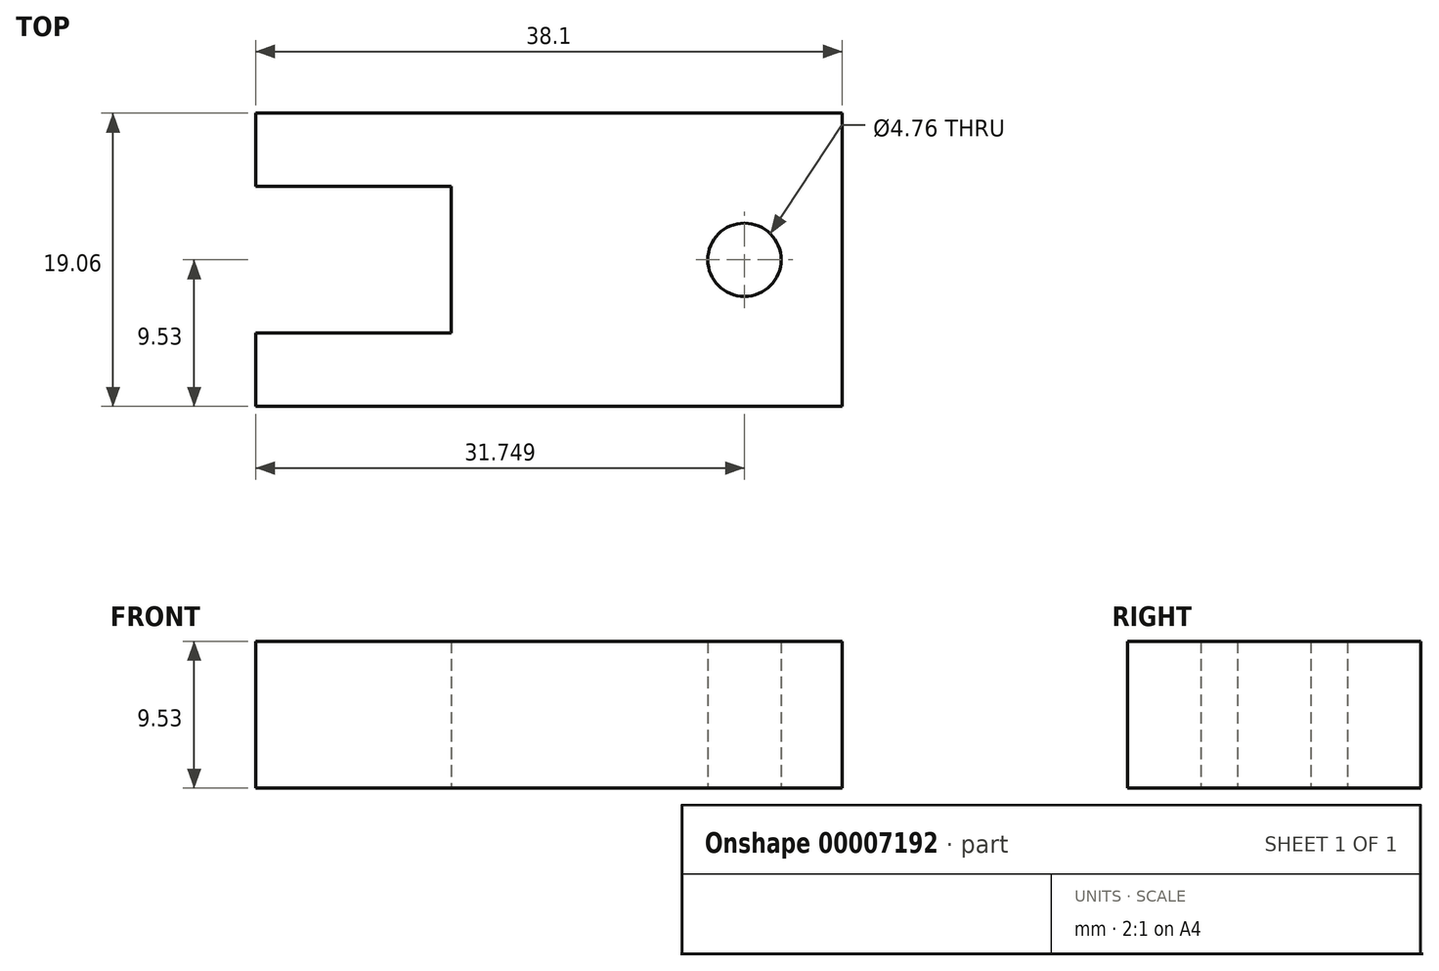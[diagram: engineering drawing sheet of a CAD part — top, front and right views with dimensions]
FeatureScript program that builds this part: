
annotation { "Feature Type Name" : "Feature", "Feature Type Description" : "" }
export const myFeature = defineFeature(function(context is Context, id is Id, definition is map)
    precondition{}
    {
        {
            var Q0;
            Q0=qCreatedBy(makeId("Top.planeOp"),FACE);
            var sketch = newSketch(context, id + "F0", { "sketchPlane" : qUnion([Q0])});
            skLineSegment(sketch, "E0", {"start": v(-14.22, 9.52) * mm, "end": v(-14.22, 4.76) * mm});
            skLineSegment(sketch, "E1", {"start": v(-14.22, 4.76) * mm, "end": v(-1.52, 4.76) * mm});
            skLineSegment(sketch, "E2", {"start": v(-1.52, 4.76) * mm, "end": v(-1.52, -4.76) * mm});
            skLineSegment(sketch, "E3", {"start": v(-1.52, -4.76) * mm, "end": v(-14.22, -4.76) * mm});
            skLineSegment(sketch, "E4", {"start": v(-14.22, -4.76) * mm, "end": v(-14.22, -9.52) * mm});
            skLineSegment(sketch, "E5", {"start": v(-14.22, -9.52) * mm, "end": v(23.88, -9.52) * mm});
            skLineSegment(sketch, "E6", {"start": v(23.88, -9.52) * mm, "end": v(23.88, 9.53) * mm});
            skLineSegment(sketch, "E7", {"start": v(23.88, 9.53) * mm, "end": v(-14.22, 9.52) * mm});
            skLineSegment(sketch, "E8", {"start": v(-23.53, 0) * mm, "end": v(23.87, 0) * mm});
            skCircle(sketch, "E9", {"center": v(17.53, 0) * mm, "radius": 2.38 * mm});
            skSolve(sketch);
        }
        {
            var Q0;
            {var subQ9=sQuery(id+"F0.wireOp",EDGE,"E3");Q0=makeQuery(id+"F0.imprint","IMPRINT",FACE,{"disambiguationData":[TD([[makeQuery(id+"F0.imprint","IMPRINT",EDGE,{"derivedFrom":subQ9}),1.0]])]});}
            var Q1;
            Q1=makeQuery(id+"F0.imprint","IMPRINT",FACE,{"disambiguationData":[TD([[makeQuery(id+"F0.imprint","IMPRINT",EDGE,{"derivedFrom":sQuery(id+"F0.wireOp",EDGE,"E0")}),1.0]])]});
            extrude(context, id + "F1", {"entities" : qUnion([Q0, Q1]), "depth" : 9.52 * mm});
        }
    });
